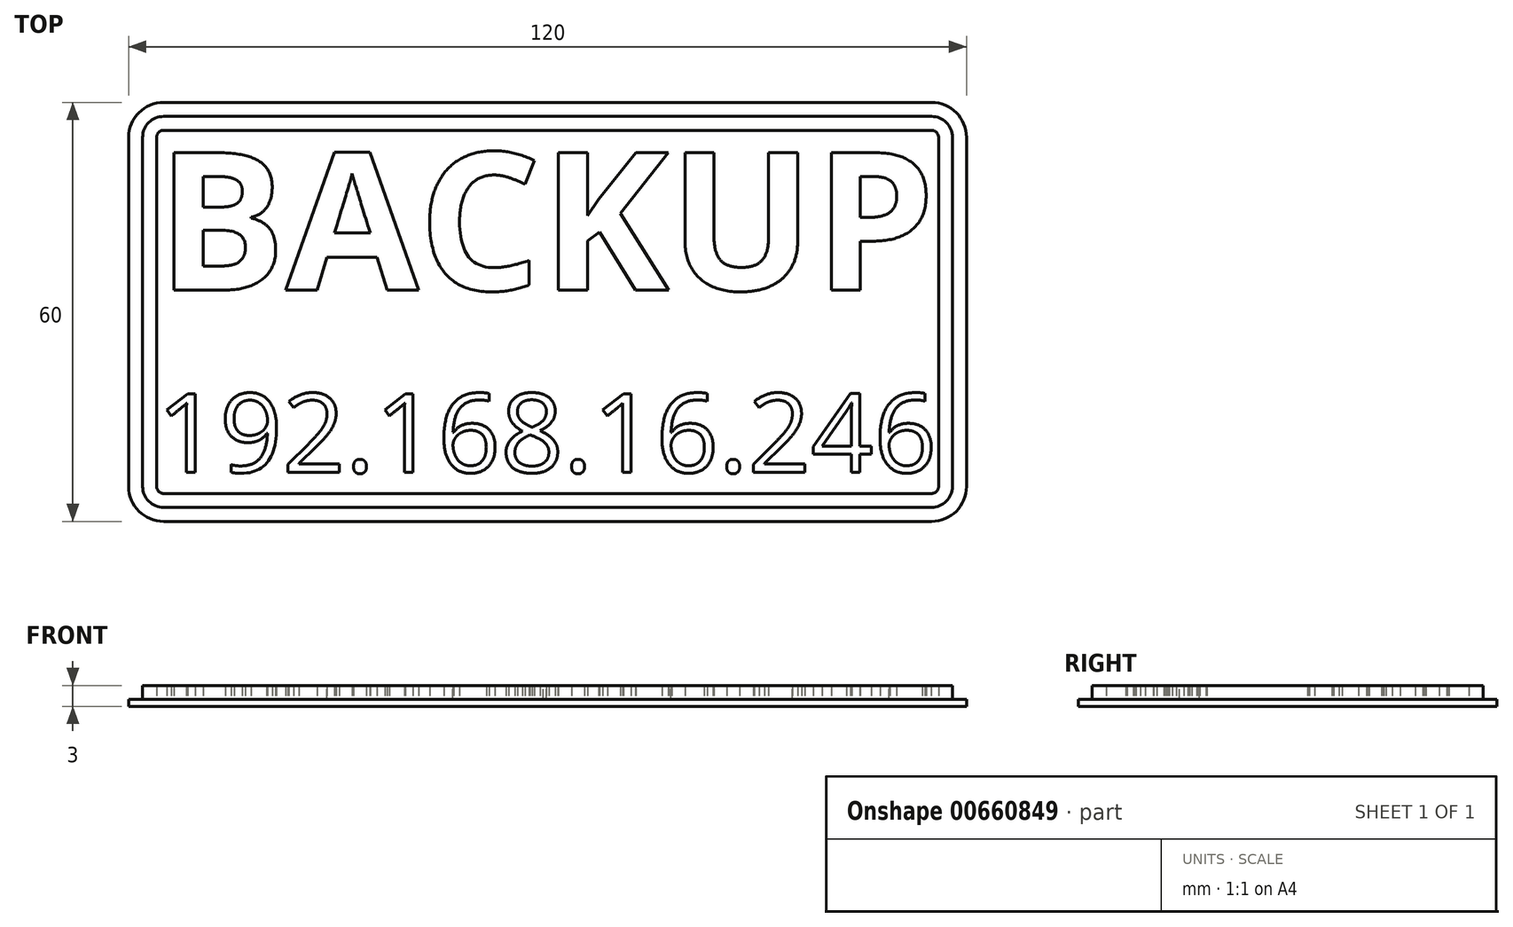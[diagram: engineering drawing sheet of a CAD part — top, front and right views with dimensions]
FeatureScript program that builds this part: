
annotation { "Feature Type Name" : "Feature", "Feature Type Description" : "" }
export const myFeature = defineFeature(function(context is Context, id is Id, definition is map)
    precondition{}
    {
        {
            assignVariable(context, id + "F0", {"variableType" : VariableType.LENGTH, "name" : "st", "lengthValue" : 1 * mm});
        }
        {
            assignVariable(context, id + "F1", {"variableType" : VariableType.LENGTH, "name" : "ft", "lengthValue" : 2 * mm});
        }
        {
            var Q0;
            Q0=qCreatedBy(makeId("Top.planeOp"),FACE);
            var sketch = newSketch(context, id + "F2", { "sketchPlane" : qUnion([Q0])});
            skLineSegment(sketch, "E0.bottom", {"start": v(-55, 30) * mm, "end": v(55, 30) * mm});
            skLineSegment(sketch, "E0.top", {"start": v(-55, -30) * mm, "end": v(55, -30) * mm});
            skLineSegment(sketch, "E0.left", {"start": v(-60, 25) * mm, "end": v(-60, -25) * mm});
            skLineSegment(sketch, "E0.right", {"start": v(60, 25) * mm, "end": v(60, -25) * mm});
            skPoint(sketch, "E1", {"position": v(0, 30) * mm});
            skPoint(sketch, "E2", {"position": v(-60, 0) * mm});
            skPoint(sketch, "E3.visualSharp", {"position": v(-60, 30) * mm});
            skArc(sketch, "E3.filletArc", {"start": v(-55, 30) * mm, "mid": v(-58.54, 28.54) * mm, "end": v(-60, 25) * mm});
            skPoint(sketch, "E4.visualSharp", {"position": v(60, 30) * mm});
            skArc(sketch, "E4.filletArc", {"start": v(60, 25) * mm, "mid": v(58.54, 28.54) * mm, "end": v(55, 30) * mm});
            skPoint(sketch, "E5.visualSharp", {"position": v(60, -30) * mm});
            skArc(sketch, "E5.filletArc", {"start": v(55, -30) * mm, "mid": v(58.54, -28.54) * mm, "end": v(60, -25) * mm});
            skPoint(sketch, "E6.visualSharp", {"position": v(-60, -30) * mm});
            skArc(sketch, "E6.filletArc", {"start": v(-60, -25) * mm, "mid": v(-58.54, -28.54) * mm, "end": v(-55, -30) * mm});
            skSolve(sketch);
        }
        {
            var Q0;
            Q0=qSketchRegion(id+"F2",true);
            extrude(context, id + "F3", {"entities" : qUnion([Q0]), "depth" : getVariable(context, 'st'), "offsetDistance" : 25 * mm});
        }
        {
            var Q0;
            Q0=makeQuery(id+"F3.opExtrude","CAP_FACE",FACE,{"disambiguationData":[OSD([sQuery(id+"F2.wireOp",EDGE,"E0.bottom"),sQuery(id+"F2.wireOp",EDGE,"E0.top"),sQuery(id+"F2.wireOp",EDGE,"E0.left"),sQuery(id+"F2.wireOp",EDGE,"E0.right"),sQuery(id+"F2.wireOp",EDGE,"E3.filletArc"),sQuery(id+"F2.wireOp",EDGE,"E4.filletArc"),sQuery(id+"F2.wireOp",EDGE,"E5.filletArc"),sQuery(id+"F2.wireOp",EDGE,"E6.filletArc")])],"isStart":false});
            var sketch = newSketch(context, id + "F4", { "sketchPlane" : qUnion([Q0])});
            skArc(sketch, "E7.0", {"start": v(-55, 28) * mm, "mid": v(-57.12, 27.12) * mm, "end": v(-58, 25) * mm});
            skLineSegment(sketch, "E7.1", {"start": v(-55, 28) * mm, "end": v(55, 28) * mm});
            skLineSegment(sketch, "E7.2", {"start": v(-58, 25) * mm, "end": v(-58, -25) * mm});
            skArc(sketch, "E7.3", {"start": v(58, 25) * mm, "mid": v(57.12, 27.12) * mm, "end": v(55, 28) * mm});
            skArc(sketch, "E7.4", {"start": v(-58, -25) * mm, "mid": v(-57.12, -27.12) * mm, "end": v(-55, -28) * mm});
            skLineSegment(sketch, "E7.5", {"start": v(-55, -28) * mm, "end": v(55, -28) * mm});
            skArc(sketch, "E7.6", {"start": v(55, -28) * mm, "mid": v(57.12, -27.12) * mm, "end": v(58, -25) * mm});
            skLineSegment(sketch, "E7.7", {"start": v(58, 25) * mm, "end": v(58, -25) * mm});
            skArc(sketch, "E8.0", {"start": v(-55, 26) * mm, "mid": v(-55.7, 25.7) * mm, "end": v(-56, 25) * mm});
            skLineSegment(sketch, "E8.1", {"start": v(-55, 26) * mm, "end": v(55, 26) * mm});
            skLineSegment(sketch, "E8.2", {"start": v(-56, 25) * mm, "end": v(-56, -25) * mm});
            skArc(sketch, "E8.3", {"start": v(56, 25) * mm, "mid": v(55.7, 25.7) * mm, "end": v(55, 26) * mm});
            skArc(sketch, "E8.4", {"start": v(-56, -25) * mm, "mid": v(-55.7, -25.7) * mm, "end": v(-55, -26) * mm});
            skLineSegment(sketch, "E8.5", {"start": v(-55, -26) * mm, "end": v(55, -26) * mm});
            skArc(sketch, "E8.6", {"start": v(55, -26) * mm, "mid": v(55.7, -25.7) * mm, "end": v(56, -25) * mm});
            skLineSegment(sketch, "E8.7", {"start": v(56, 25) * mm, "end": v(56, -25) * mm});
            skText(sketch, "E9", { "text": "BACKUP", "fontName": "OpenSans-Bold.ttf"});
            skText(sketch, "E10", { "text": "192.168.16.246", "fontName": "OpenSans-Regular.ttf"});
            skLineSegment(sketch, "E11", {"start": v(0, -22.96) * mm, "end": v(0, 22.96) * mm, "construction": true});
            const initialGuessF4  = {"E9": [-0.056, 0.00314, 1, 0, 0.01983], "E10": [-0.056, -0.02296, 1, 0, 0.01135]};
            skSetInitialGuess(sketch, initialGuessF4);
            skSolve(sketch);
        }
        {
            var Q0;
            Q0=makeQuery(id+"F4.imprint","IMPRINT",FACE,{"disambiguationData":[TD([[makeQuery(id+"F4.imprint","IMPRINT",EDGE,{"derivedFrom":sQuery(id+"F4.wireOp",EDGE,"E10.sketch_text.stroke-215")}),-1.0]])]});
            var Q1;
            Q1=makeQuery(id+"F4.imprint","IMPRINT",FACE,{"disambiguationData":[TD([[makeQuery(id+"F4.imprint","IMPRINT",EDGE,{"derivedFrom":sQuery(id+"F4.wireOp",EDGE,"E10.sketch_text.stroke-198")}),-1.0]])]});
            var Q2;
            Q2=makeQuery(id+"F4.imprint","IMPRINT",FACE,{"disambiguationData":[TD([[makeQuery(id+"F4.imprint","IMPRINT",EDGE,{"derivedFrom":sQuery(id+"F4.wireOp",EDGE,"E10.sketch_text.stroke-178")}),-1.0]])]});
            var Q3;
            Q3=makeQuery(id+"F4.imprint","IMPRINT",FACE,{"disambiguationData":[TD([[makeQuery(id+"F4.imprint","IMPRINT",EDGE,{"derivedFrom":sQuery(id+"F4.wireOp",EDGE,"E10.sketch_text.stroke-170")}),-1.0]])]});
            var Q4;
            Q4=makeQuery(id+"F4.imprint","IMPRINT",FACE,{"disambiguationData":[TD([[makeQuery(id+"F4.imprint","IMPRINT",EDGE,{"derivedFrom":sQuery(id+"F4.wireOp",EDGE,"E10.sketch_text.stroke-145")}),-1.0]])]});
            var Q5;
            Q5=makeQuery(id+"F4.imprint","IMPRINT",FACE,{"disambiguationData":[TD([[makeQuery(id+"F4.imprint","IMPRINT",EDGE,{"derivedFrom":sQuery(id+"F4.wireOp",EDGE,"E10.sketch_text.stroke-136")}),-1.0]])]});
            var Q6;
            Q6=makeQuery(id+"F4.imprint","IMPRINT",FACE,{"disambiguationData":[TD([[makeQuery(id+"F4.imprint","IMPRINT",EDGE,{"derivedFrom":sQuery(id+"F4.wireOp",EDGE,"E10.sketch_text.stroke-128")}),-1.0]])]});
            var Q7;
            Q7=makeQuery(id+"F4.imprint","IMPRINT",FACE,{"disambiguationData":[TD([[makeQuery(id+"F4.imprint","IMPRINT",EDGE,{"derivedFrom":sQuery(id+"F4.wireOp",EDGE,"E10.sketch_text.stroke-97")}),-1.0]])]});
            var Q8;
            Q8=makeQuery(id+"F4.imprint","IMPRINT",FACE,{"disambiguationData":[TD([[makeQuery(id+"F4.imprint","IMPRINT",EDGE,{"derivedFrom":sQuery(id+"F4.wireOp",EDGE,"E10.sketch_text.stroke-72")}),-1.0]])]});
            var Q9;
            Q9=makeQuery(id+"F4.imprint","IMPRINT",FACE,{"disambiguationData":[TD([[makeQuery(id+"F4.imprint","IMPRINT",EDGE,{"derivedFrom":sQuery(id+"F4.wireOp",EDGE,"E10.sketch_text.stroke-0")}),-1.0]])]});
            var Q10;
            Q10=makeQuery(id+"F4.imprint","IMPRINT",FACE,{"disambiguationData":[TD([[makeQuery(id+"F4.imprint","IMPRINT",EDGE,{"derivedFrom":sQuery(id+"F4.wireOp",EDGE,"E10.sketch_text.stroke-9")}),-1.0]])]});
            var Q11;
            Q11=makeQuery(id+"F4.imprint","IMPRINT",FACE,{"disambiguationData":[TD([[makeQuery(id+"F4.imprint","IMPRINT",EDGE,{"derivedFrom":sQuery(id+"F4.wireOp",EDGE,"E10.sketch_text.stroke-35")}),-1.0]])]});
            var Q12;
            Q12=makeQuery(id+"F4.imprint","IMPRINT",FACE,{"disambiguationData":[TD([[makeQuery(id+"F4.imprint","IMPRINT",EDGE,{"derivedFrom":sQuery(id+"F4.wireOp",EDGE,"E10.sketch_text.stroke-55")}),-1.0]])]});
            var Q13;
            Q13=makeQuery(id+"F4.imprint","IMPRINT",FACE,{"disambiguationData":[TD([[makeQuery(id+"F4.imprint","IMPRINT",EDGE,{"derivedFrom":sQuery(id+"F4.wireOp",EDGE,"E10.sketch_text.stroke-63")}),-1.0]])]});
            var Q14;
            Q14=makeQuery(id+"F4.imprint","IMPRINT",FACE,{"disambiguationData":[TD([[makeQuery(id+"F4.imprint","IMPRINT",EDGE,{"derivedFrom":sQuery(id+"F4.wireOp",EDGE,"E9.sketch_text.stroke-0")}),-1.0]])]});
            var Q15;
            Q15=makeQuery(id+"F4.imprint","IMPRINT",FACE,{"disambiguationData":[TD([[makeQuery(id+"F4.imprint","IMPRINT",EDGE,{"derivedFrom":sQuery(id+"F4.wireOp",EDGE,"E7.0")}),1.0]])]});
            var Q16;
            Q16=makeQuery(id+"F4.imprint","IMPRINT",FACE,{"disambiguationData":[TD([[makeQuery(id+"F4.imprint","IMPRINT",EDGE,{"derivedFrom":sQuery(id+"F4.wireOp",EDGE,"E9.sketch_text.stroke-13")}),-1.0]])]});
            var Q17;
            Q17=makeQuery(id+"F4.imprint","IMPRINT",FACE,{"disambiguationData":[TD([[makeQuery(id+"F4.imprint","IMPRINT",EDGE,{"derivedFrom":sQuery(id+"F4.wireOp",EDGE,"E9.sketch_text.stroke-41")}),-1.0]])]});
            var Q18;
            Q18=makeQuery(id+"F4.imprint","IMPRINT",FACE,{"disambiguationData":[TD([[makeQuery(id+"F4.imprint","IMPRINT",EDGE,{"derivedFrom":sQuery(id+"F4.wireOp",EDGE,"E9.sketch_text.stroke-45")}),-1.0]])]});
            var Q19;
            Q19=makeQuery(id+"F4.imprint","IMPRINT",FACE,{"disambiguationData":[TD([[makeQuery(id+"F4.imprint","IMPRINT",EDGE,{"derivedFrom":sQuery(id+"F4.wireOp",EDGE,"E9.sketch_text.stroke-57")}),-1.0]])]});
            var Q20;
            Q20=makeQuery(id+"F4.imprint","IMPRINT",FACE,{"disambiguationData":[TD([[makeQuery(id+"F4.imprint","IMPRINT",EDGE,{"derivedFrom":sQuery(id+"F4.wireOp",EDGE,"E9.sketch_text.stroke-76")}),-1.0]])]});
            var Q21;
            Q21=makeQuery(id+"F4.imprint","IMPRINT",FACE,{"disambiguationData":[TD([[makeQuery(id+"F4.imprint","IMPRINT",EDGE,{"derivedFrom":sQuery(id+"F4.wireOp",EDGE,"E9.sketch_text.stroke-25")}),-1.0]])]});
            var Q22;
            Q22=makeQuery(id+"F4.imprint","IMPRINT",FACE,{"disambiguationData":[TD([[makeQuery(id+"F4.imprint","IMPRINT",EDGE,{"derivedFrom":sQuery(id+"F4.wireOp",EDGE,"E9.sketch_text.stroke-80")}),-1.0]])]});
            extrude(context, id + "F5", {"entities" : qUnion([Q0, Q1, Q2, Q3, Q4, Q5, Q6, Q7, Q8, Q9, Q10, Q11, Q12, Q13, Q14, Q15, Q16, Q17, Q18, Q19, Q20, Q21, Q22]), "operationType" : NewBodyOperationType.ADD, "depth" : getVariable(context, 'ft'), "offsetDistance" : 25 * mm});
        }
    });
